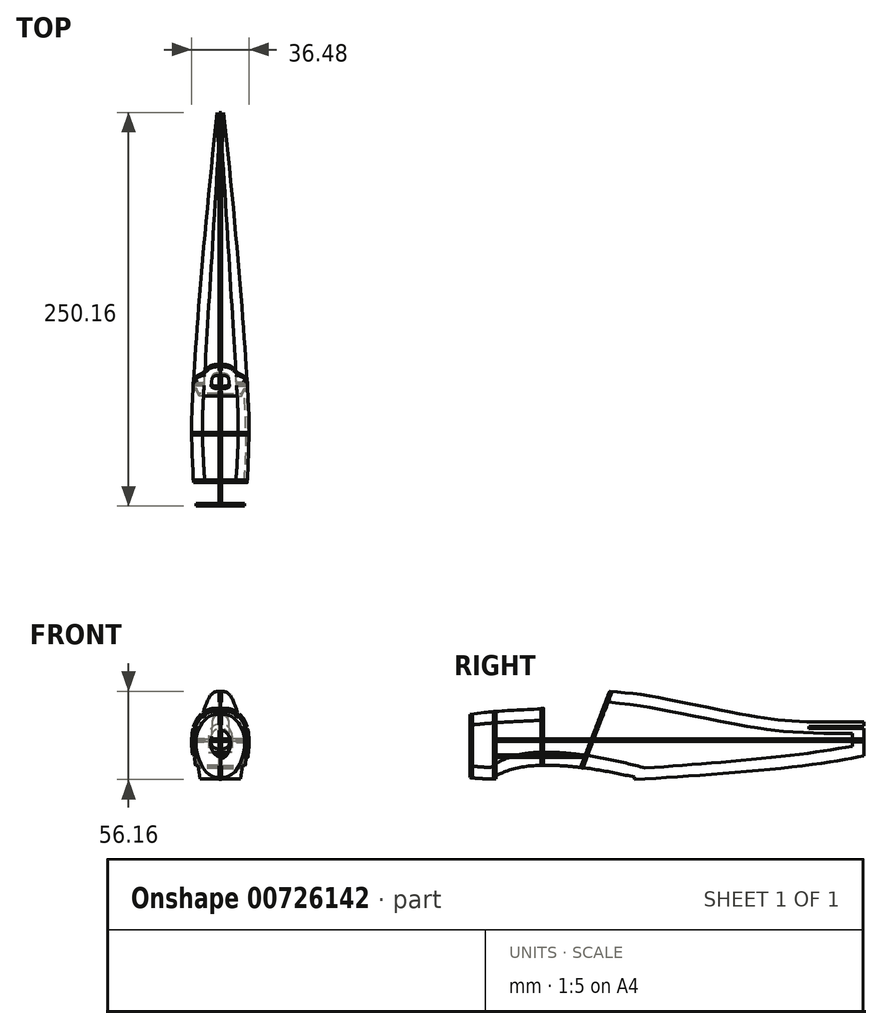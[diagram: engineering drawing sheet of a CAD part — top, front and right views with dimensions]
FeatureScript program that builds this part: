
annotation { "Feature Type Name" : "Feature", "Feature Type Description" : "" }
export const myFeature = defineFeature(function(context is Context, id is Id, definition is map)
    precondition{}
    {
        {
            var Q0;
            Q0=qCreatedBy(makeId("Front.planeOp"),FACE);
            var sketch = newSketch(context, id + "F0", { "sketchPlane" : qUnion([Q0])});
            skLineSegment(sketch, "E0", {"start": v(-45.72, -81.03) * mm, "end": v(-45.72, 42.74) * mm});
            skLineSegment(sketch, "E1", {"start": v(0, 8.5) * mm, "end": v(0, 11.22) * mm});
            skLineSegment(sketch, "E2", {"start": v(0, 8.5) * mm, "end": v(0.8, 8.5) * mm});
            skLineSegment(sketch, "E3", {"start": v(0.8, 8.5) * mm, "end": v(0.8, 0) * mm});
            skLineSegment(sketch, "E4", {"start": v(0.8, 0) * mm, "end": v(15.19, 0) * mm});
            skLineSegment(sketch, "E5", {"start": v(15.19, 0) * mm, "end": v(16, 6.79) * mm});
            skLineSegment(sketch, "E6", {"start": v(16, 6.79) * mm, "end": v(17.73, 6.79) * mm});
            skLineSegment(sketch, "E7", {"start": v(0, 26.26) * mm, "end": v(0, 28.64) * mm});
            skLineSegment(sketch, "E8", {"start": v(0, 28.64) * mm, "end": v(0.8, 28.64) * mm});
            skLineSegment(sketch, "E9", {"start": v(0.8, 28.64) * mm, "end": v(0.8, 36.2) * mm});
            skFitSpline(sketch, "E10", {"points": [v(0.8, 36.2) * mm, v(4.42, 36.2) * mm, v(7.03, 35.67) * mm, v(10.45, 34.08) * mm, v(13.7, 31.07) * mm, v(15.93, 27.53) * mm, v(17.68, 22) * mm, v(18.14, 17.58) * mm, v(18.16, 12.03) * mm, v(17.73, 6.79) * mm], "startDerivative": vector(37.72, 1.34) * mm, "endDerivative": vector(-4.49, -42.1) * mm});
            skArc(sketch, "E11", {"start": v(0, 11.22) * mm, "mid": v(7.52, 18.74) * mm, "end": v(0, 26.26) * mm});
            skLineSegment(sketch, "E12", {"start": v(12.27, 32.61) * mm, "end": v(11.23, 31.4) * mm});
            skLineSegment(sketch, "E13", {"start": v(11.23, 31.4) * mm, "end": v(10.03, 32.44) * mm});
            skLineSegment(sketch, "E14", {"start": v(10.03, 32.44) * mm, "end": v(11.06, 33.64) * mm});
            skLineSegment(sketch, "E15", {"start": v(16.99, 24.71) * mm, "end": v(15.46, 24.28) * mm});
            skLineSegment(sketch, "E16", {"start": v(15.46, 24.28) * mm, "end": v(15.89, 22.76) * mm});
            skLineSegment(sketch, "E17", {"start": v(15.89, 22.76) * mm, "end": v(17.42, 23.19) * mm});
            skLineSegment(sketch, "E18", {"start": v(18.16, 16.74) * mm, "end": v(11.35, 16.74) * mm});
            skLineSegment(sketch, "E19", {"start": v(11.35, 16.74) * mm, "end": v(11.35, 15.15) * mm});
            skLineSegment(sketch, "E20", {"start": v(11.35, 15.15) * mm, "end": v(18.2, 15.15) * mm});
            skSolve(sketch);
        }
        {
            var Q0;
            Q0=qCreatedBy(makeId("Right.planeOp"),FACE);
            var sketch = newSketch(context, id + "F1", { "sketchPlane" : qUnion([Q0])});
            skLineSegment(sketch, "E21", {"start": v(-46.82, 25.55) * mm, "end": v(-46.82, 32.46) * mm});
            skLineSegment(sketch, "E22", {"start": v(0, 28.65) * mm, "end": v(0, 35.89) * mm});
            skFitSpline(sketch, "E23", {"points": [v(-46.82, 32.46) * mm, v(-26.41, 34.55) * mm, v(0, 35.89) * mm], "startDerivative": vector(62.7, 7.8) * mm, "endDerivative": vector(51.3, 1.96) * mm});
            skFitSpline(sketch, "E24", {"points": [v(-46.82, 25.55) * mm, v(-28.77, 27.19) * mm, v(0, 28.65) * mm], "startDerivative": vector(38.42, 3.94) * mm, "endDerivative": vector(54.6, 2.32) * mm});
            skLineSegment(sketch, "E25", {"start": v(-46.82, -7.7) * mm, "end": v(-46.82, -0.43) * mm});
            skLineSegment(sketch, "E26", {"start": v(-30.25, -8.48) * mm, "end": v(-30.25, -6.61) * mm});
            skLineSegment(sketch, "E27", {"start": v(57.68, -9.04) * mm, "end": v(57.68, -7.4) * mm});
            skLineSegment(sketch, "E28", {"start": v(39.27, 40.36) * mm, "end": v(41.86, 47.12) * mm});
            skLineSegment(sketch, "E29", {"start": v(203.34, 6.07) * mm, "end": v(203.34, 14.77) * mm});
            skLineSegment(sketch, "E30", {"start": v(203.34, 14.77) * mm, "end": v(196.18, 14.77) * mm});
            skLineSegment(sketch, "E31", {"start": v(196.18, 14.77) * mm, "end": v(196.18, 12.13) * mm});
            skFitSpline(sketch, "E32", {"points": [v(-46.82, -7.7) * mm, v(-41.42, -8.32) * mm, v(-36.72, -8.48) * mm, v(-30.25, -8.48) * mm], "startDerivative": vector(16.78, -2.16) * mm, "endDerivative": vector(18.74, 0.06) * mm});
            skFitSpline(sketch, "E33", {"points": [v(-46.82, -0.43) * mm, v(-42.47, -0.78) * mm, v(-38.11, -1.13) * mm, v(-33.48, -1.23) * mm], "startDerivative": vector(13.22, -1) * mm, "endDerivative": vector(13.75, -0.1) * mm});
            skFitSpline(sketch, "E34", {"points": [v(-33.48, -1.23) * mm, v(-29.01, 1.84) * mm, v(-21.3, 5.24) * mm, v(-12.18, 7.41) * mm, v(0.38, 8.37) * mm, v(21.7, 7) * mm, v(44.32, 3.22) * mm, v(64.43, -1.67) * mm], "startDerivative": vector(45.31, 34.36) * mm, "endDerivative": vector(112.32, -29) * mm});
            skFitSpline(sketch, "E35", {"points": [v(64.43, -1.67) * mm, v(113.62, 2.1) * mm, v(164.91, 7.32) * mm, v(196.18, 12.13) * mm], "startDerivative": vector(135.8, 9.82) * mm, "endDerivative": vector(102.63, 17.34) * mm});
            skFitSpline(sketch, "E36", {"points": [v(-30.25, -6.61) * mm, v(-26.4, -4.72) * mm, v(-17.92, -1.96) * mm, v(-6.74, -0.22) * mm, v(10.88, -0.2) * mm, v(34.26, -2.84) * mm, v(57.68, -7.4) * mm], "startDerivative": vector(37.04, 20.06) * mm, "endDerivative": vector(106.35, -22.44) * mm});
            skFitSpline(sketch, "E37", {"points": [v(57.68, -9.04) * mm, v(102.95, -6.05) * mm, v(153.96, -1.43) * mm, v(186.9, 3) * mm, v(203.34, 6.07) * mm], "startDerivative": vector(155.37, 9.52) * mm, "endDerivative": vector(88.38, 17.58) * mm});
            skFitSpline(sketch, "E38", {"points": [v(41.86, 47.12) * mm, v(63.38, 44.68) * mm, v(94.56, 38.76) * mm, v(130.9, 31.61) * mm, v(149.2, 28.87) * mm, v(167.13, 27.5) * mm], "startDerivative": vector(111.24, -10.3) * mm, "endDerivative": vector(107.82, -6.76) * mm});
            skLineSegment(sketch, "E39", {"start": v(167.13, 27.5) * mm, "end": v(203.34, 27.5) * mm});
            skLineSegment(sketch, "E40", {"start": v(203.34, 27.5) * mm, "end": v(203.34, 25.2) * mm});
            skLineSegment(sketch, "E41", {"start": v(203.34, 25.2) * mm, "end": v(168.53, 24.89) * mm});
            skLineSegment(sketch, "E42", {"start": v(168.53, 24.89) * mm, "end": v(168.54, 23.2) * mm});
            skLineSegment(sketch, "E43", {"start": v(168.54, 23.2) * mm, "end": v(203.34, 23.52) * mm});
            skLineSegment(sketch, "E44", {"start": v(203.34, 23.52) * mm, "end": v(203.34, 14.77) * mm});
            skLineSegment(sketch, "E45", {"start": v(196.18, 14.77) * mm, "end": v(196.18, 20.27) * mm});
            skFitSpline(sketch, "E46", {"points": [v(196.18, 20.27) * mm, v(174.38, 20.53) * mm, v(151.26, 21.68) * mm, v(133.08, 24.2) * mm, v(91.61, 32.11) * mm, v(65.77, 37.05) * mm, v(39.27, 40.36) * mm], "startDerivative": vector(-139.03, 0.7) * mm, "endDerivative": vector(-171.57, 17) * mm});
            skSolve(sketch);
        }
        {
            var Q0;
            Q0=makeQuery(id+"F1.imprint","IMPRINT",FACE,{"disambiguationData":[TD([[makeQuery(id+"F1.imprint","IMPRINT",EDGE,{"derivedFrom":sQuery(id+"F1.wireOp",EDGE,"E21")}),-1.0]])]});
            var Q1;
            Q1=makeQuery(id+"F1.imprint","IMPRINT",FACE,{"disambiguationData":[TD([[makeQuery(id+"F1.imprint","IMPRINT",EDGE,{"derivedFrom":sQuery(id+"F1.wireOp",EDGE,"E28")}),-1.0]])]});
            extrude(context, id + "F2", {"entities" : qUnion([Q0, Q1]), "depth" : 1.59 * mm, "offsetDistance" : 25.4 * mm, "symmetric" : true});
        }
        {
            var Q0;
            Q0=makeQuery(id+"F1.imprint","IMPRINT",FACE,{"disambiguationData":[TD([[makeQuery(id+"F1.imprint","IMPRINT",EDGE,{"derivedFrom":sQuery(id+"F1.wireOp",EDGE,"E25")}),-1.0]])]});
            extrude(context, id + "F3", {"entities" : qUnion([Q0]), "depth" : 1.59 * mm, "offsetDistance" : 25.4 * mm, "symmetric" : true});
        }
        {
            var Q0;
            Q0=makeQuery(id+"F0.imprint","IMPRINT",FACE,{"disambiguationData":[TD([[makeQuery(id+"F0.imprint","IMPRINT",EDGE,{"derivedFrom":sQuery(id+"F0.wireOp",EDGE,"E1")}),-1.0]])]});
            extrude(context, id + "F4", {"entities" : qUnion([Q0]), "depth" : 1.59 * mm, "offsetDistance" : 25.4 * mm});
        }
        {
            var Q0;
            Q0=qCreatedBy(makeId("Front.planeOp"),FACE);
            cPlane(context, id + "F5", {"entities" : qUnion([Q0]), "cplaneType" : CPlaneType.OFFSET, "offset" : 30.23 * mm, "width" : 152.4 * mm, "height" : 152.4 * mm});
        }
        {
            var Q0;
            Q0=qCreatedBy(id+"F5.planeOp",FACE);
            var sketch = newSketch(context, id + "F6", { "sketchPlane" : qUnion([Q0])});
            skLineSegment(sketch, "E47", {"start": v(-109.7, 0) * mm, "end": v(-109.7, 61.64) * mm});
            skLineSegment(sketch, "E48", {"start": v(0.8, 27.08) * mm, "end": v(0.8, 34.27) * mm});
            skLineSegment(sketch, "E49", {"start": v(0.8, 27.08) * mm, "end": v(-0.8, 27.08) * mm});
            skLineSegment(sketch, "E50", {"start": v(0.8, -6.6) * mm, "end": v(0.8, 1.1) * mm});
            skLineSegment(sketch, "E51", {"start": v(0.8, 1.1) * mm, "end": v(-0.8, 1.1) * mm});
            skLineSegment(sketch, "E52.0", {"start": v(0.8, -8.48) * mm, "end": v(-0.8, -8.48) * mm});
            skLineSegment(sketch, "E53", {"start": v(0.8, -6.6) * mm, "end": v(0.8, -8.48) * mm});
            skLineSegment(sketch, "E54", {"start": v(0.8, -8.48) * mm, "end": v(12.86, -8.48) * mm});
            skLineSegment(sketch, "E55", {"start": v(12.86, -8.48) * mm, "end": v(14.22, 0.05) * mm});
            skLineSegment(sketch, "E56", {"start": v(14.22, 0.05) * mm, "end": v(15.81, -0.2) * mm});
            skLineSegment(sketch, "E57", {"start": v(0, 27.08) * mm, "end": v(0, 23.97) * mm});
            skLineSegment(sketch, "E58", {"start": v(0, 1.1) * mm, "end": v(0, 5.48) * mm});
            skEllipticalArc(sketch, "E59", {});
            skFitSpline(sketch, "E60", {"points": [v(0.8, 34.27) * mm, v(7.36, 33.57) * mm, v(13.61, 28.58) * mm, v(16.68, 20) * mm, v(16.99, 10.9) * mm, v(15.81, -0.2) * mm], "startDerivative": vector(38.09, 0.59) * mm, "endDerivative": vector(-6.4, -50.41) * mm});
            skLineSegment(sketch, "E61", {"start": v(16.63, 6.7) * mm, "end": v(15.06, 6.87) * mm});
            skLineSegment(sketch, "E62", {"start": v(15.06, 6.87) * mm, "end": v(14.88, 5.3) * mm});
            skLineSegment(sketch, "E63", {"start": v(14.88, 5.3) * mm, "end": v(16.46, 5.13) * mm});
            skLineSegment(sketch, "E64", {"start": v(15.66, 24.35) * mm, "end": v(14.13, 23.9) * mm});
            skLineSegment(sketch, "E65", {"start": v(14.13, 23.9) * mm, "end": v(14.58, 22.37) * mm});
            skLineSegment(sketch, "E66", {"start": v(14.58, 22.37) * mm, "end": v(16.1, 22.82) * mm});
            skLineSegment(sketch, "E67", {"start": v(9.91, 32.27) * mm, "end": v(8.95, 31) * mm});
            skLineSegment(sketch, "E68", {"start": v(8.95, 31) * mm, "end": v(10.21, 30.04) * mm});
            skLineSegment(sketch, "E69", {"start": v(10.21, 30.04) * mm, "end": v(11.18, 31.3) * mm});
            skLineSegment(sketch, "E70", {"start": v(17.03, 16.73) * mm, "end": v(9.88, 16.73) * mm});
            skLineSegment(sketch, "E71", {"start": v(9.88, 16.73) * mm, "end": v(9.88, 15.14) * mm});
            skLineSegment(sketch, "E72", {"start": v(9.88, 15.14) * mm, "end": v(17.09, 15.14) * mm});
            const initialGuessF6  = {"E59": [0, 0.014726084191352129, 0, 1, 0.009245883207768202, 0.006289035926070388, 3.141592653589793, 0]};
            skSetInitialGuess(sketch, initialGuessF6);
            skSolve(sketch);
        }
        {
            var Q0;
            {var subQ9=sQuery(id+"F6.wireOp",EDGE,"E48");Q0=makeQuery(id+"F6.imprint","IMPRINT",FACE,{"disambiguationData":[TD([[makeQuery(id+"F6.imprint","IMPRINT",EDGE,{"derivedFrom":subQ9}),-1.0]])]});}
            extrude(context, id + "F7", {"entities" : qUnion([Q0]), "depth" : 1.59 * mm, "offsetDistance" : 25.4 * mm});
        }
        {
            var Q0;
            Q0=makeQuery(id+"F2.opExtrude","SWEPT_FACE",FACE,{"disambiguationData":[OSD([sQuery(id+"F1.wireOp",EDGE,"E28")])]});
            cPlane(context, id + "F8", {"entities" : qUnion([Q0]), "cplaneType" : CPlaneType.OFFSET, "offset" : 0 * mm, "width" : 152.4 * mm, "height" : 152.4 * mm});
        }
        {
            var Q0;
            Q0=qCreatedBy(id+"F8.planeOp",FACE);
            var sketch = newSketch(context, id + "F9", { "sketchPlane" : qUnion([Q0])});
            skLineSegment(sketch, "E73", {"start": v(-66.8, -71.12) * mm, "end": v(-66.8, 47.64) * mm});
            skLineSegment(sketch, "E74", {"start": v(0.8, 51.73) * mm, "end": v(0.8, 58.97) * mm});
            skLineSegment(sketch, "E75", {"start": v(-0.8, 51.73) * mm, "end": v(0.8, 51.73) * mm});
            skLineSegment(sketch, "E76", {"start": v(0.8, 15.38) * mm, "end": v(-0.8, 15.38) * mm});
            skLineSegment(sketch, "E77", {"start": v(0.8, 7.12) * mm, "end": v(0.8, 15.38) * mm});
            skLineSegment(sketch, "E78", {"start": v(0, 15.38) * mm, "end": v(0, 19.8) * mm});
            skLineSegment(sketch, "E79", {"start": v(0, 19.8) * mm, "end": v(1.5, 19.8) * mm});
            skLineSegment(sketch, "E80", {"start": v(0, 51.73) * mm, "end": v(0, 43.4) * mm});
            skLineSegment(sketch, "E81", {"start": v(0, 43.4) * mm, "end": v(0.88, 43.4) * mm});
            skLineSegment(sketch, "E82", {"start": v(5.19, 38.37) * mm, "end": v(5.8, 24.31) * mm});
            skArc(sketch, "E83", {"start": v(1.5, 19.8) * mm, "mid": v(4.61, 21.14) * mm, "end": v(5.8, 24.31) * mm});
            skFitSpline(sketch, "E84", {"points": [v(0.88, 43.4) * mm, v(2.94, 42.94) * mm, v(4.66, 40.66) * mm, v(5.19, 38.37) * mm], "startDerivative": vector(6.6, 0) * mm, "endDerivative": vector(0.26, -5.87) * mm});
            skLineSegment(sketch, "E85", {"start": v(0.8, 7.12) * mm, "end": v(13.46, 7.12) * mm});
            skLineSegment(sketch, "E86", {"start": v(13.46, 7.12) * mm, "end": v(15.06, 16.23) * mm});
            skLineSegment(sketch, "E87", {"start": v(15.06, 16.23) * mm, "end": v(16.5, 15.98) * mm});
            skFitSpline(sketch, "E88", {"points": [v(0.8, 58.97) * mm, v(3.58, 58.35) * mm, v(5.97, 56.45) * mm, v(8.16, 52.28) * mm, v(10.24, 46.6) * mm, v(10.62, 45.37) * mm, v(12.1, 42.22) * mm, v(13.5, 40.51) * mm, v(15.05, 38) * mm, v(15.97, 35.77) * mm, v(16.86, 31.33) * mm, v(17.2, 22.86) * mm, v(16.5, 15.98) * mm], "startDerivative": vector(50.6, -0.16) * mm, "endDerivative": vector(-8.19, -58.54) * mm});
            skLineSegment(sketch, "E89", {"start": v(11.04, 44.3) * mm, "end": v(9.6, 43.63) * mm});
            skLineSegment(sketch, "E90", {"start": v(9.6, 43.63) * mm, "end": v(10.3, 42.2) * mm});
            skLineSegment(sketch, "E91", {"start": v(10.3, 42.2) * mm, "end": v(11.72, 42.88) * mm});
            skLineSegment(sketch, "E92", {"start": v(16.26, 34.7) * mm, "end": v(14.71, 34.37) * mm});
            skLineSegment(sketch, "E93", {"start": v(14.71, 34.37) * mm, "end": v(15.03, 32.82) * mm});
            skLineSegment(sketch, "E94", {"start": v(15.03, 32.82) * mm, "end": v(16.59, 33.14) * mm});
            skLineSegment(sketch, "E95", {"start": v(17.22, 26.37) * mm, "end": v(10.35, 26.37) * mm});
            skLineSegment(sketch, "E96", {"start": v(10.35, 26.37) * mm, "end": v(10.35, 24.78) * mm});
            skLineSegment(sketch, "E97", {"start": v(10.35, 24.78) * mm, "end": v(17.24, 24.78) * mm});
            skSolve(sketch);
        }
        {
            var Q0;
            {var subQ8=sQuery(id+"F9.wireOp",EDGE,"E74");Q0=makeQuery(id+"F9.imprint","IMPRINT",FACE,{"disambiguationData":[TD([[makeQuery(id+"F9.imprint","IMPRINT",EDGE,{"derivedFrom":subQ8}),-1.0]])]});}
            extrude(context, id + "F10", {"entities" : qUnion([Q0]), "oppositeDirection" : true, "depth" : 1.59 * mm, "offsetDistance" : 25.4 * mm});
        }
        {
            var Q0;
            Q0=makeQuery(id+"F7.opExtrude","SWEPT_BODY",BODY,{"disambiguationData":[OSD([sQuery(id+"F6.wireOp",EDGE,"E48"),sQuery(id+"F6.wireOp",EDGE,"E49"),sQuery(id+"F6.wireOp",EDGE,"E50"),sQuery(id+"F6.wireOp",EDGE,"E51"),sQuery(id+"F6.wireOp",EDGE,"E53"),sQuery(id+"F6.wireOp",EDGE,"E54"),sQuery(id+"F6.wireOp",EDGE,"E55"),sQuery(id+"F6.wireOp",EDGE,"E56"),sQuery(id+"F6.wireOp",EDGE,"E57"),sQuery(id+"F6.wireOp",EDGE,"E58"),sQuery(id+"F6.wireOp",EDGE,"E59"),sQuery(id+"F6.wireOp",EDGE,"E60"),sQuery(id+"F6.wireOp",EDGE,"E61"),sQuery(id+"F6.wireOp",EDGE,"E62"),sQuery(id+"F6.wireOp",EDGE,"E63"),sQuery(id+"F6.wireOp",EDGE,"E64"),sQuery(id+"F6.wireOp",EDGE,"E65"),sQuery(id+"F6.wireOp",EDGE,"E66"),sQuery(id+"F6.wireOp",EDGE,"E67"),sQuery(id+"F6.wireOp",EDGE,"E68"),sQuery(id+"F6.wireOp",EDGE,"E69"),sQuery(id+"F6.wireOp",EDGE,"E70"),sQuery(id+"F6.wireOp",EDGE,"E71"),sQuery(id+"F6.wireOp",EDGE,"E72")])]});
            var Q1;
            Q1=qCreatedBy(makeId("Right.planeOp"),FACE);
            mirror(context, id + "F11", {"entities" : qUnion([Q0]), "mirrorPlane" : qUnion([Q1])});
        }
        {
            var Q0;
            Q0=makeQuery(id+"F4.opExtrude","SWEPT_BODY",BODY,{"disambiguationData":[OSD([sQuery(id+"F0.wireOp",EDGE,"E1"),sQuery(id+"F0.wireOp",EDGE,"E2"),sQuery(id+"F0.wireOp",EDGE,"E3"),sQuery(id+"F0.wireOp",EDGE,"E4"),sQuery(id+"F0.wireOp",EDGE,"E5"),sQuery(id+"F0.wireOp",EDGE,"E6"),sQuery(id+"F0.wireOp",EDGE,"E7"),sQuery(id+"F0.wireOp",EDGE,"E8"),sQuery(id+"F0.wireOp",EDGE,"E9"),sQuery(id+"F0.wireOp",EDGE,"E10"),sQuery(id+"F0.wireOp",EDGE,"E11"),sQuery(id+"F0.wireOp",EDGE,"E12"),sQuery(id+"F0.wireOp",EDGE,"E13"),sQuery(id+"F0.wireOp",EDGE,"E14"),sQuery(id+"F0.wireOp",EDGE,"E15"),sQuery(id+"F0.wireOp",EDGE,"E16"),sQuery(id+"F0.wireOp",EDGE,"E17"),sQuery(id+"F0.wireOp",EDGE,"E18"),sQuery(id+"F0.wireOp",EDGE,"E19"),sQuery(id+"F0.wireOp",EDGE,"E20")])]});
            var Q1;
            Q1=qCreatedBy(makeId("Right.planeOp"),FACE);
            mirror(context, id + "F12", {"entities" : qUnion([Q0]), "mirrorPlane" : qUnion([Q1])});
        }
        {
            var Q0;
            Q0=makeQuery(id+"F10.opExtrude","SWEPT_BODY",BODY,{"disambiguationData":[OSD([sQuery(id+"F9.wireOp",EDGE,"E74"),sQuery(id+"F9.wireOp",EDGE,"E75"),sQuery(id+"F9.wireOp",EDGE,"E76"),sQuery(id+"F9.wireOp",EDGE,"E77"),sQuery(id+"F9.wireOp",EDGE,"E78"),sQuery(id+"F9.wireOp",EDGE,"E79"),sQuery(id+"F9.wireOp",EDGE,"E80"),sQuery(id+"F9.wireOp",EDGE,"E81"),sQuery(id+"F9.wireOp",EDGE,"E82"),sQuery(id+"F9.wireOp",EDGE,"E83"),sQuery(id+"F9.wireOp",EDGE,"E84"),sQuery(id+"F9.wireOp",EDGE,"E85"),sQuery(id+"F9.wireOp",EDGE,"E86"),sQuery(id+"F9.wireOp",EDGE,"E87"),sQuery(id+"F9.wireOp",EDGE,"E88"),sQuery(id+"F9.wireOp",EDGE,"E89"),sQuery(id+"F9.wireOp",EDGE,"E90"),sQuery(id+"F9.wireOp",EDGE,"E91"),sQuery(id+"F9.wireOp",EDGE,"E92"),sQuery(id+"F9.wireOp",EDGE,"E93"),sQuery(id+"F9.wireOp",EDGE,"E94"),sQuery(id+"F9.wireOp",EDGE,"E95"),sQuery(id+"F9.wireOp",EDGE,"E96"),sQuery(id+"F9.wireOp",EDGE,"E97")])]});
            var Q1;
            Q1=qCreatedBy(makeId("Right.planeOp"),FACE);
            mirror(context, id + "F13", {"entities" : qUnion([Q0]), "mirrorPlane" : qUnion([Q1])});
        }
        {
            var Q0;
            Q0=makeQuery(id+"F4.opExtrude","SWEPT_FACE",FACE,{"disambiguationData":[OSD([sQuery(id+"F0.wireOp",EDGE,"E20")])]});
            cPlane(context, id + "F14", {"entities" : qUnion([Q0]), "cplaneType" : CPlaneType.OFFSET, "offset" : 0 * mm, "width" : 152.4 * mm, "height" : 152.4 * mm});
        }
        {
            var Q0;
            Q0=qCreatedBy(id+"F14.planeOp",FACE);
            var sketch = newSketch(context, id + "F15", { "sketchPlane" : qUnion([Q0])});
            skLineSegment(sketch, "E98", {"start": v(9.88, -31.81) * mm, "end": v(9.88, -30.23) * mm});
            skLineSegment(sketch, "E99", {"start": v(11.35, -1.59) * mm, "end": v(11.35, 0) * mm});
            skLineSegment(sketch, "E100", {"start": v(10.35, 31.32) * mm, "end": v(10.35, 29.73) * mm});
            skPoint(sketch, "E101.0", {"position": v(17.09, -31.81) * mm});
            skPoint(sketch, "E102.0", {"position": v(18.2, -1.59) * mm});
            skPoint(sketch, "E103.0", {"position": v(17.24, 29.64) * mm});
            skFitSpline(sketch, "E104", {"points": [v(17.09, -31.81) * mm, v(18.2, -1.59) * mm, v(17.24, 29.64) * mm, v(1.96, 203.22) * mm], "startDerivative": vector(6.32, 139.97) * mm, "endDerivative": vector(-43.2, 382.48) * mm});
            skFitSpline(sketch, "E105", {"points": [v(9.88, -31.81) * mm, v(11.35, -1.59) * mm, v(10.35, 29.73) * mm, v(1.1, 180.92) * mm], "startDerivative": vector(8.42, 134.31) * mm, "endDerivative": vector(-21.44, 343.34) * mm});
            skLineSegment(sketch, "E106", {"start": v(9.88, -31.81) * mm, "end": v(17.09, -31.81) * mm});
            skLineSegment(sketch, "E107", {"start": v(1.1, 180.92) * mm, "end": v(1.96, 203.22) * mm});
            skSolve(sketch);
        }
        {
            var Q0;
            Q0 = qSketchRegion(id + "F15", true);
            extrude(context, id + "F16", {"entities" : qUnion([Q0]), "depth" : 1.59 * mm, "offsetDistance" : 25.4 * mm});
        }
        {
            var Q0;
            Q0=makeQuery(id+"F16.opExtrude","SWEPT_BODY",BODY,{"disambiguationData":[OSD([sQuery(id+"F15.wireOp",EDGE,"E104"),sQuery(id+"F15.wireOp",EDGE,"E105"),sQuery(id+"F15.wireOp",EDGE,"E106"),sQuery(id+"F15.wireOp",EDGE,"E107")])]});
            var Q1;
            Q1=qCreatedBy(makeId("Right.planeOp"),FACE);
            mirror(context, id + "F17", {"entities" : qUnion([Q0]), "mirrorPlane" : qUnion([Q1])});
        }
        {
            var Q0;
            Q0=makeQuery(id+"F4.opExtrude","SWEPT_FACE",FACE,{"disambiguationData":[OSD([sQuery(id+"F0.wireOp",EDGE,"E6")])]});
            cPlane(context, id + "F18", {"entities" : qUnion([Q0]), "cplaneType" : CPlaneType.OFFSET, "offset" : 0 * mm, "width" : 152.4 * mm, "height" : 152.4 * mm});
        }
        {
            var Q0;
            Q0=qCreatedBy(id+"F18.planeOp",FACE);
            var sketch = newSketch(context, id + "F19", { "sketchPlane" : qUnion([Q0])});
            skPoint(sketch, "E108.0", {"position": v(16.63, 31.81) * mm});
            skPoint(sketch, "E109.0", {"position": v(17.73, 1.59) * mm});
            skPoint(sketch, "E110.0", {"position": v(16.5, -26.49) * mm});
            skFitSpline(sketch, "E111", {"points": [v(16.63, 31.81) * mm, v(17.73, 1.59) * mm, v(16.5, -26.49) * mm], "startDerivative": vector(5.35, -59.88) * mm, "endDerivative": vector(-4.04, -56.7) * mm});
            skFitSpline(sketch, "E112.0", {"points": [v(15.05, 31.67) * mm, v(15.5, 26.71) * mm, v(16.09, 16.79) * mm, v(16.24, 2.07) * mm, v(15.82, -12.25) * mm, v(15.25, -21.66) * mm, v(14.91, -26.38) * mm]});
            skLineSegment(sketch, "E113", {"start": v(16.63, 31.81) * mm, "end": v(15.05, 31.67) * mm});
            skLineSegment(sketch, "E114", {"start": v(16.5, -26.49) * mm, "end": v(14.91, -26.38) * mm});
            skSolve(sketch);
        }
        {
            var Q0;
            Q0 = qSketchRegion(id + "F19", true);
            extrude(context, id + "F20", {"entities" : qUnion([Q0]), "depth" : 1.59 * mm, "offsetDistance" : 25.4 * mm});
        }
        {
            var Q0;
            Q0=makeQuery(id+"F3.opExtrude","SWEPT_EDGE",EDGE,{"disambiguationData":[OSD([sQuery(id+"F1.wireOp",EDGE,"E25"),sQuery(id+"F1.wireOp",EDGE,"E32")])]});
            cPoint(context, id + "F21", {"entities" : qUnion([Q0]), "parameter" : 0.5});
        }
        {
            var Q0;
            Q0=makeQuery(id+"F2.opExtrude","CAP_VERTEX",VERTEX,{"disambiguationData":[OSD([sQuery(id+"F1.wireOp",EDGE,"E21"),sQuery(id+"F1.wireOp",EDGE,"E23")])],"isStart":true});
            var Q1;
            Q1=makeQuery(id+"F2.opExtrude","CAP_VERTEX",VERTEX,{"disambiguationData":[OSD([sQuery(id+"F1.wireOp",EDGE,"E21"),sQuery(id+"F1.wireOp",EDGE,"E23")])],"isStart":false});
            var Q2;
            Q2 = qCreatedBy(id + "F21" ,VERTEX);
            cPlane(context, id + "F22", {"entities" : qUnion([Q0, Q1, Q2]), "cplaneType" : CPlaneType.THREE_POINT, "offset" : 25.4 * mm, "width" : 152.4 * mm, "height" : 152.4 * mm});
        }
        {
            var Q0;
            Q0=qCreatedBy(id+"F22.planeOp",FACE);
            var sketch = newSketch(context, id + "F23", { "sketchPlane" : qUnion([Q0])});
            skLineSegment(sketch, "E115", {"start": v(-6.35, -82.55) * mm, "end": v(-6.35, 52.2) * mm});
            skLineSegment(sketch, "E116", {"start": v(0.8, 25.55) * mm, "end": v(0.8, 32.46) * mm});
            skLineSegment(sketch, "E117", {"start": v(0.8, 25.55) * mm, "end": v(-0.8, 25.55) * mm});
            skLineSegment(sketch, "E118", {"start": v(0.8, -7.7) * mm, "end": v(0.8, -0.43) * mm});
            skLineSegment(sketch, "E119", {"start": v(0.8, -0.43) * mm, "end": v(-0.8, -0.43) * mm});
            skFitSpline(sketch, "E120", {"points": [v(0.8, 32.46) * mm, v(7.96, 30.54) * mm, v(12.31, 25.8) * mm, v(15.24, 17.83) * mm, v(14.8, 8.13) * mm, v(8.74, -4.5) * mm, v(0.8, -7.7) * mm], "startDerivative": vector(66.78, 0.28) * mm, "endDerivative": vector(-42, 0.3) * mm});
            skLineSegment(sketch, "E121", {"start": v(0, 25.55) * mm, "end": v(0, 22.24) * mm});
            skLineSegment(sketch, "E122", {"start": v(0, -0.43) * mm, "end": v(0, 4.12) * mm});
            skFitSpline(sketch, "E123", {"points": [v(0, 22.24) * mm, v(2.26, 21.82) * mm, v(5.12, 19.33) * mm, v(6.38, 15.2) * mm, v(6.09, 10.7) * mm, v(3.88, 6.33) * mm, v(0, 4.12) * mm], "startDerivative": vector(18.36, -0.31) * mm, "endDerivative": vector(-20.91, -0.02) * mm});
            skSolve(sketch);
        }
        {
            var Q0;
            Q0 = qSketchRegion(id + "F23", true);
            extrude(context, id + "F24", {"entities" : qUnion([Q0]), "oppositeDirection" : true, "depth" : 1.59 * mm, "offsetDistance" : 25.4 * mm});
        }
        {
            var Q0;
            Q0=makeQuery(id+"F24.opExtrude","SWEPT_BODY",BODY,{"disambiguationData":[OSD([sQuery(id+"F23.wireOp",EDGE,"E116"),sQuery(id+"F23.wireOp",EDGE,"E117"),sQuery(id+"F23.wireOp",EDGE,"E118"),sQuery(id+"F23.wireOp",EDGE,"E119"),sQuery(id+"F23.wireOp",EDGE,"E120"),sQuery(id+"F23.wireOp",EDGE,"E121"),sQuery(id+"F23.wireOp",EDGE,"E122"),sQuery(id+"F23.wireOp",EDGE,"E123")])]});
            var Q1;
            Q1=qCreatedBy(makeId("Right.planeOp"),FACE);
            mirror(context, id + "F25", {"entities" : qUnion([Q0]), "mirrorPlane" : qUnion([Q1])});
        }
        {
            var Q0;
            Q0=makeQuery(id+"F24.opExtrude","CAP_FACE",FACE,{"disambiguationData":[OSD([sQuery(id+"F23.wireOp",EDGE,"E116"),sQuery(id+"F23.wireOp",EDGE,"E117"),sQuery(id+"F23.wireOp",EDGE,"E118"),sQuery(id+"F23.wireOp",EDGE,"E119"),sQuery(id+"F23.wireOp",EDGE,"E120"),sQuery(id+"F23.wireOp",EDGE,"E121"),sQuery(id+"F23.wireOp",EDGE,"E122"),sQuery(id+"F23.wireOp",EDGE,"E123")])],"isStart":true});
            var sketch = newSketch(context, id + "F26", { "sketchPlane" : qUnion([Q0])});
            skPoint(sketch, "E124", {"position": v(0, 15.95) * mm});
            skPoint(sketch, "E125.0", {"position": v(-1.1, 15.95) * mm});
            skSolve(sketch);
        }
        {
            var Q0;
            Q0=makeQuery(id+"F4.opExtrude","CAP_FACE",FACE,{"disambiguationData":[OSD([sQuery(id+"F0.wireOp",EDGE,"E1"),sQuery(id+"F0.wireOp",EDGE,"E2"),sQuery(id+"F0.wireOp",EDGE,"E3"),sQuery(id+"F0.wireOp",EDGE,"E4"),sQuery(id+"F0.wireOp",EDGE,"E5"),sQuery(id+"F0.wireOp",EDGE,"E6"),sQuery(id+"F0.wireOp",EDGE,"E7"),sQuery(id+"F0.wireOp",EDGE,"E8"),sQuery(id+"F0.wireOp",EDGE,"E9"),sQuery(id+"F0.wireOp",EDGE,"E10"),sQuery(id+"F0.wireOp",EDGE,"E11"),sQuery(id+"F0.wireOp",EDGE,"E12"),sQuery(id+"F0.wireOp",EDGE,"E13"),sQuery(id+"F0.wireOp",EDGE,"E14"),sQuery(id+"F0.wireOp",EDGE,"E15"),sQuery(id+"F0.wireOp",EDGE,"E16"),sQuery(id+"F0.wireOp",EDGE,"E17"),sQuery(id+"F0.wireOp",EDGE,"E18"),sQuery(id+"F0.wireOp",EDGE,"E19"),sQuery(id+"F0.wireOp",EDGE,"E20")])],"isStart":true});
            var sketch = newSketch(context, id + "F27", { "sketchPlane" : qUnion([Q0])});
            skLineSegment(sketch, "E126.bottom", {"start": v(-7.52, 18.74) * mm, "end": v(0, 18.74) * mm});
            skLineSegment(sketch, "E126.top", {"start": v(-7.52, 8.28) * mm, "end": v(0, 8.28) * mm});
            skLineSegment(sketch, "E126.left", {"start": v(-7.52, 18.74) * mm, "end": v(-7.52, 8.28) * mm});
            skLineSegment(sketch, "E126.right", {"start": v(0, 18.74) * mm, "end": v(0, 8.28) * mm});
            skSolve(sketch);
        }
        {
            var Q0;
            Q0 = qSketchRegion(id + "F27", true);
            var Q1;
            Q1=makeQuery(id+"F4.opExtrude","CAP_FACE",FACE,{"disambiguationData":[OSD([sQuery(id+"F0.wireOp",EDGE,"E1"),sQuery(id+"F0.wireOp",EDGE,"E2"),sQuery(id+"F0.wireOp",EDGE,"E3"),sQuery(id+"F0.wireOp",EDGE,"E4"),sQuery(id+"F0.wireOp",EDGE,"E5"),sQuery(id+"F0.wireOp",EDGE,"E6"),sQuery(id+"F0.wireOp",EDGE,"E7"),sQuery(id+"F0.wireOp",EDGE,"E8"),sQuery(id+"F0.wireOp",EDGE,"E9"),sQuery(id+"F0.wireOp",EDGE,"E10"),sQuery(id+"F0.wireOp",EDGE,"E11"),sQuery(id+"F0.wireOp",EDGE,"E12"),sQuery(id+"F0.wireOp",EDGE,"E13"),sQuery(id+"F0.wireOp",EDGE,"E14"),sQuery(id+"F0.wireOp",EDGE,"E15"),sQuery(id+"F0.wireOp",EDGE,"E16"),sQuery(id+"F0.wireOp",EDGE,"E17"),sQuery(id+"F0.wireOp",EDGE,"E18"),sQuery(id+"F0.wireOp",EDGE,"E19"),sQuery(id+"F0.wireOp",EDGE,"E20")])],"isStart":false});
            extrude(context, id + "F28", {"entities" : qUnion([Q0]), "operationType" : NewBodyOperationType.REMOVE, "endBound" : BoundingType.UP_TO_SURFACE, "oppositeDirection" : true, "depth" : 25 * mm, "endBoundEntityFace" : qUnion([Q1]), "offsetDistance" : 25 * mm});
        }
        {
            var Q0;
            Q0=makeQuery(id+"F12.opPattern","COPY",FACE,{"derivedFrom":makeQuery(id+"F4.opExtrude","CAP_FACE",FACE,{"disambiguationData":[OSD([sQuery(id+"F0.wireOp",EDGE,"E1"),sQuery(id+"F0.wireOp",EDGE,"E2"),sQuery(id+"F0.wireOp",EDGE,"E3"),sQuery(id+"F0.wireOp",EDGE,"E4"),sQuery(id+"F0.wireOp",EDGE,"E5"),sQuery(id+"F0.wireOp",EDGE,"E6"),sQuery(id+"F0.wireOp",EDGE,"E7"),sQuery(id+"F0.wireOp",EDGE,"E8"),sQuery(id+"F0.wireOp",EDGE,"E9"),sQuery(id+"F0.wireOp",EDGE,"E10"),sQuery(id+"F0.wireOp",EDGE,"E11"),sQuery(id+"F0.wireOp",EDGE,"E12"),sQuery(id+"F0.wireOp",EDGE,"E13"),sQuery(id+"F0.wireOp",EDGE,"E14"),sQuery(id+"F0.wireOp",EDGE,"E15"),sQuery(id+"F0.wireOp",EDGE,"E16"),sQuery(id+"F0.wireOp",EDGE,"E17"),sQuery(id+"F0.wireOp",EDGE,"E18"),sQuery(id+"F0.wireOp",EDGE,"E19"),sQuery(id+"F0.wireOp",EDGE,"E20")])],"isStart":true}),"instanceName":"1"});
            var sketch = newSketch(context, id + "F29", { "sketchPlane" : qUnion([Q0])});
            skLineSegment(sketch, "E127.bottom", {"start": v(7.52, 18.74) * mm, "end": v(0, 18.74) * mm});
            skLineSegment(sketch, "E127.top", {"start": v(7.52, 8.23) * mm, "end": v(0, 8.23) * mm});
            skLineSegment(sketch, "E127.left", {"start": v(7.52, 18.74) * mm, "end": v(7.52, 8.23) * mm});
            skLineSegment(sketch, "E127.right", {"start": v(0, 18.74) * mm, "end": v(0, 8.23) * mm});
            skSolve(sketch);
        }
        {
            var Q0;
            Q0 = qSketchRegion(id + "F29", true);
            var Q1;
            Q1=makeQuery(id+"F12.opPattern","COPY",FACE,{"derivedFrom":makeQuery(id+"F4.opExtrude","CAP_FACE",FACE,{"disambiguationData":[OSD([sQuery(id+"F0.wireOp",EDGE,"E1"),sQuery(id+"F0.wireOp",EDGE,"E2"),sQuery(id+"F0.wireOp",EDGE,"E3"),sQuery(id+"F0.wireOp",EDGE,"E4"),sQuery(id+"F0.wireOp",EDGE,"E5"),sQuery(id+"F0.wireOp",EDGE,"E6"),sQuery(id+"F0.wireOp",EDGE,"E7"),sQuery(id+"F0.wireOp",EDGE,"E8"),sQuery(id+"F0.wireOp",EDGE,"E9"),sQuery(id+"F0.wireOp",EDGE,"E10"),sQuery(id+"F0.wireOp",EDGE,"E11"),sQuery(id+"F0.wireOp",EDGE,"E12"),sQuery(id+"F0.wireOp",EDGE,"E13"),sQuery(id+"F0.wireOp",EDGE,"E14"),sQuery(id+"F0.wireOp",EDGE,"E15"),sQuery(id+"F0.wireOp",EDGE,"E16"),sQuery(id+"F0.wireOp",EDGE,"E17"),sQuery(id+"F0.wireOp",EDGE,"E18"),sQuery(id+"F0.wireOp",EDGE,"E19"),sQuery(id+"F0.wireOp",EDGE,"E20")])],"isStart":false}),"instanceName":"1"});
            extrude(context, id + "F30", {"entities" : qUnion([Q0]), "operationType" : NewBodyOperationType.REMOVE, "endBound" : BoundingType.UP_TO_SURFACE, "oppositeDirection" : true, "depth" : 25 * mm, "endBoundEntityFace" : qUnion([Q1]), "offsetDistance" : 25 * mm});
        }
    });
